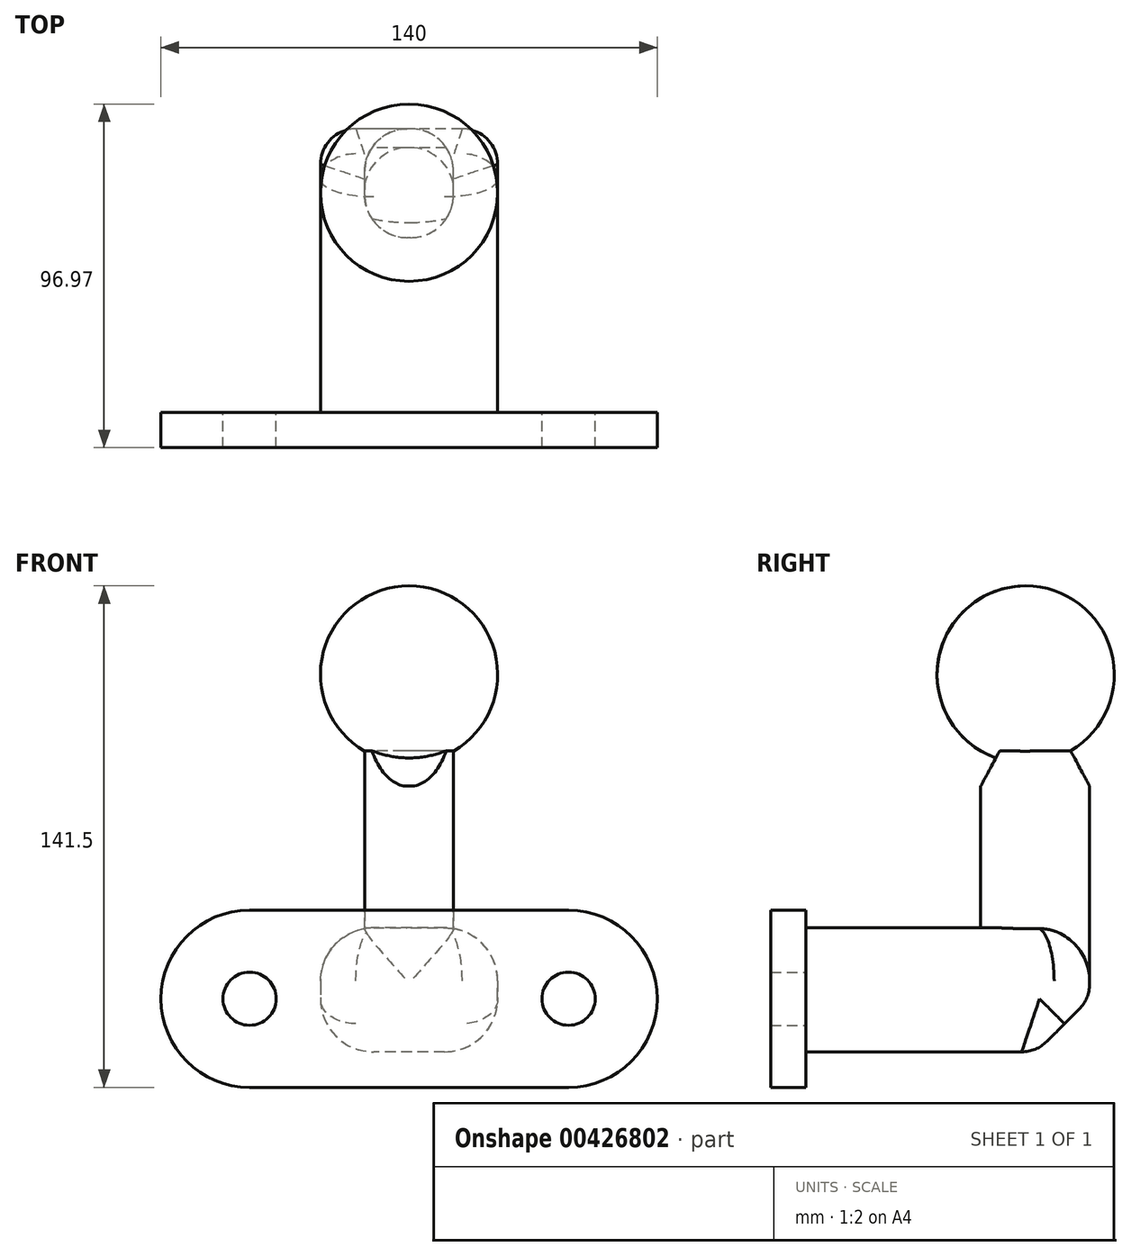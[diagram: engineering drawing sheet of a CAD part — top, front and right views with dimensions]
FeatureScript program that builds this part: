
annotation { "Feature Type Name" : "Feature", "Feature Type Description" : "" }
export const myFeature = defineFeature(function(context is Context, id is Id, definition is map)
    precondition{}
    {
        {
            var Q0;
            Q0=qCreatedBy(makeId("Front.planeOp"),FACE);
            var sketch = newSketch(context, id + "F0", { "sketchPlane" : qUnion([Q0])});
            skLineSegment(sketch, "E0.bottom", {"start": v(-45, 25) * mm, "end": v(45, 25) * mm});
            skLineSegment(sketch, "E0.top", {"start": v(-45, -25) * mm, "end": v(45, -25) * mm});
            skLineSegment(sketch, "E0.left", {"start": v(-70, 0) * mm, "end": v(-70, 0) * mm});
            skLineSegment(sketch, "E0.right", {"start": v(70, 0) * mm, "end": v(70, 0) * mm});
            skPoint(sketch, "E0.middle", {"position": v(0, 0) * mm});
            skCircle(sketch, "E1", {"center": v(-45, 0) * mm, "radius": 7.5 * mm});
            skCircle(sketch, "E2", {"center": v(45, 0) * mm, "radius": 7.5 * mm});
            skPoint(sketch, "E3.visualSharp", {"position": v(-70, 25) * mm});
            skArc(sketch, "E3.filletArc", {"start": v(-45, 25) * mm, "mid": v(-62.68, 17.68) * mm, "end": v(-70, 0) * mm});
            skPoint(sketch, "E4.visualSharp", {"position": v(-70, -25) * mm});
            skArc(sketch, "E4.filletArc", {"start": v(-70, 0) * mm, "mid": v(-62.68, -17.68) * mm, "end": v(-45, -25) * mm});
            skPoint(sketch, "E5.visualSharp", {"position": v(70, -25) * mm});
            skArc(sketch, "E5.filletArc", {"start": v(45, -25) * mm, "mid": v(62.68, -17.68) * mm, "end": v(70, 0) * mm});
            skPoint(sketch, "E6.visualSharp", {"position": v(70, 25) * mm});
            skArc(sketch, "E6.filletArc", {"start": v(70, 0) * mm, "mid": v(62.68, 17.68) * mm, "end": v(45, 25) * mm});
            skSolve(sketch);
        }
        {
            var Q0;
            Q0=makeQuery(id+"F0.imprint","IMPRINT",FACE,{"disambiguationData":[TD([[makeQuery(id+"F0.imprint","IMPRINT",EDGE,{"derivedFrom":sQuery(id+"F0.wireOp",EDGE,"E0.bottom")}),-1.0]])]});
            extrude(context, id + "F1", {"entities" : qUnion([Q0]), "depth" : 10 * mm});
        }
        {
            var Q0;
            Q0=qCreatedBy(makeId("Right.planeOp"),FACE);
            var sketch = newSketch(context, id + "F2", { "sketchPlane" : qUnion([Q0])});
            skLineSegment(sketch, "E7.bottom", {"start": v(0, 20) * mm, "end": v(80, 20) * mm});
            skLineSegment(sketch, "E7.top", {"start": v(0, -15) * mm, "end": v(80, -15) * mm});
            skLineSegment(sketch, "E7.left", {"start": v(0, 20) * mm, "end": v(0, -15) * mm});
            skLineSegment(sketch, "E7.right", {"start": v(80, 20) * mm, "end": v(80, -15) * mm});
            skLineSegment(sketch, "E8", {"start": v(80, 20) * mm, "end": v(80, 60) * mm});
            skLineSegment(sketch, "E9", {"start": v(64.64, 92.1) * mm, "end": v(64.64, 12.06) * mm, "construction": true});
            skLineSegment(sketch, "E10.MirrorCS", {"start": v(49.28, 20) * mm, "end": v(49.28, 60) * mm});
            skLineSegment(sketch, "E11", {"start": v(54.64, 70) * mm, "end": v(74.64, 70) * mm});
            skLineSegment(sketch, "E12", {"start": v(74.64, 70) * mm, "end": v(80, 60) * mm});
            skLineSegment(sketch, "E13", {"start": v(49.28, 60) * mm, "end": v(54.64, 70) * mm});
            skSolve(sketch);
        }
        {
            var Q0;
            Q0=makeQuery(id+"F2.imprint","IMPRINT",FACE,{"disambiguationData":[TD([[makeQuery(id+"F2.imprint","IMPRINT",EDGE,{"derivedFrom":sQuery(id+"F2.wireOp",EDGE,"E7.top")}),1.0]])]});
            extrude(context, id + "F3", {"entities" : qUnion([Q0]), "operationType" : NewBodyOperationType.ADD, "endBound" : BoundingType.SYMMETRIC, "depth" : 50 * mm});
        }
        {
            var Q0;
            Q0 = qSketchRegion(id + "F2", true);
            extrude(context, id + "F4", {"entities" : qUnion([Q0]), "operationType" : NewBodyOperationType.ADD, "endBound" : BoundingType.SYMMETRIC, "depth" : 25 * mm});
        }
        {
            var Q0;
            Q0=qCreatedBy(makeId("Right.planeOp"),FACE);
            var sketch = newSketch(context, id + "F5", { "sketchPlane" : qUnion([Q0])});
            skLineSegment(sketch, "E14", {"start": v(61.97, 66.5) * mm, "end": v(61.97, 91.5) * mm});
            skArc(sketch, "E15", {"start": v(61.97, 66.5) * mm, "mid": v(86.97, 91.5) * mm, "end": v(61.97, 116.5) * mm});
            skLineSegment(sketch, "E16", {"start": v(61.97, 91.5) * mm, "end": v(61.97, 116.5) * mm});
            skSolve(sketch);
        }
        {
            var Q0;
            Q0=makeQuery(id+"F5.imprint","IMPRINT",FACE,{"disambiguationData":[TD([[makeQuery(id+"F5.imprint","IMPRINT",EDGE,{"derivedFrom":sQuery(id+"F5.wireOp",EDGE,"E14")}),-1.0]])]});
            var Q1;
            Q1=sQuery(id+"F5.wireOp",EDGE,"E16");
            revolve(context, id + "F6", {"operationType" : NewBodyOperationType.ADD, "entities" : qUnion([Q0]), "axis" : qUnion([Q1]), "revolveType" : RevolveType.FULL});
        }
        {
            var Q0;
            Q0=makeQuery(id+"F4.opExtrude","CAP_EDGE",EDGE,{"disambiguationData":[OSD([sQuery(id+"F2.wireOp",EDGE,"E7.right"),sQuery(id+"F2.wireOp",EDGE,"E8")])],"isStart":true});
            var Q1;
            Q1=makeQuery(id+"F4.opExtrude","CAP_EDGE",EDGE,{"disambiguationData":[OSD([sQuery(id+"F2.wireOp",EDGE,"E7.right"),sQuery(id+"F2.wireOp",EDGE,"E8")])],"isStart":false});
            var Q2;
            Q2=makeQuery(id+"F4.opExtrude","CAP_EDGE",EDGE,{"disambiguationData":[OSD([sQuery(id+"F2.wireOp",EDGE,"E10.MirrorCS")])],"isStart":true});
            var Q3;
            Q3=makeQuery(id+"F4.opExtrude","CAP_EDGE",EDGE,{"disambiguationData":[OSD([sQuery(id+"F2.wireOp",EDGE,"E10.MirrorCS")])],"isStart":false});
            fillet(context, id + "F7", {"entities" : qUnion([Q0, Q1, Q2, Q3]), "radius" : 12 * mm, "tangentPropagation" : true, "allowEdgeOverflow" : false});
        }
        {
            var Q0;
            Q0=makeQuery(id+"F3.opExtrude","SWEPT_EDGE",EDGE,{"disambiguationData":[OSD([sQuery(id+"F2.wireOp",EDGE,"E7.top"),sQuery(id+"F2.wireOp",EDGE,"E7.right")])]});
            chamfer(context, id + "F8", {"entities" : qUnion([Q0]), "width" : 15 * mm, "tangentPropagation" : true});
        }
        {
            var Q0;
            {var subQ0=sQuery(id+"F2.wireOp",EDGE,"E7.right");Q0=makeQuery(id+"F8.opChamfer","BLEND_EDGE",EDGE,{"blendedFrom":[makeQuery(id+"F3.opExtrude","SWEPT_EDGE",EDGE,{"disambiguationData":[OSD([sQuery(id+"F2.wireOp",EDGE,"E7.top"),subQ0])]}),makeQuery(id+"F4.boolean.opBoolean","MERGE",FACE,{"derivedFrom":[makeQuery(id+"F3.opExtrude","SWEPT_FACE",FACE,{"disambiguationData":[OSD([subQ0])]}),makeQuery(id+"F4.opExtrude","SWEPT_FACE",FACE,{"disambiguationData":[OSD([subQ0,sQuery(id+"F2.wireOp",EDGE,"E8")])]})]})],"blendedInto":[makeQuery(id+"F4.boolean.opBoolean","MERGE",FACE,{"derivedFrom":[makeQuery(id+"F3.opExtrude","SWEPT_FACE",FACE,{"disambiguationData":[OSD([subQ0])]}),makeQuery(id+"F4.opExtrude","SWEPT_FACE",FACE,{"disambiguationData":[OSD([subQ0,sQuery(id+"F2.wireOp",EDGE,"E8")])]})]})]});}
            var Q1;
            {var subQ0=sQuery(id+"F2.wireOp",EDGE,"E7.top");Q1=makeQuery(id+"F8.opChamfer","BLEND_EDGE",EDGE,{"blendedFrom":[makeQuery(id+"F3.opExtrude","SWEPT_EDGE",EDGE,{"disambiguationData":[OSD([subQ0,sQuery(id+"F2.wireOp",EDGE,"E7.right")])]}),makeQuery(id+"F3.opExtrude","SWEPT_FACE",FACE,{"disambiguationData":[OSD([subQ0])]})],"blendedInto":[makeQuery(id+"F3.opExtrude","SWEPT_FACE",FACE,{"disambiguationData":[OSD([subQ0])]})]});}
            var Q2;
            Q2=makeQuery(id+"F3.opExtrude","CAP_EDGE",EDGE,{"disambiguationData":[OSD([sQuery(id+"F2.wireOp",EDGE,"E7.right")])],"isStart":false});
            var Q3;
            Q3=makeQuery(id+"F3.opExtrude","CAP_EDGE",EDGE,{"disambiguationData":[OSD([sQuery(id+"F2.wireOp",EDGE,"E7.right")])],"isStart":true});
            var Q4;
            {var subQ0=sQuery(id+"F2.wireOp",EDGE,"E7.right");var subQ1=sQuery(id+"F2.wireOp",EDGE,"E7.top");Q4=makeQuery(id+"F8.opChamfer","BLEND_EDGE",EDGE,{"blendedFrom":[makeQuery(id+"F3.opExtrude","SWEPT_EDGE",EDGE,{"disambiguationData":[OSD([subQ1,subQ0])]}),makeQuery(id+"F3.opExtrude","CAP_FACE",FACE,{"disambiguationData":[OSD([sQuery(id+"F2.wireOp",EDGE,"E7.bottom"),subQ1,sQuery(id+"F2.wireOp",EDGE,"E7.left"),subQ0])],"isStart":true})],"blendedInto":[makeQuery(id+"F3.opExtrude","CAP_FACE",FACE,{"disambiguationData":[OSD([sQuery(id+"F2.wireOp",EDGE,"E7.bottom"),subQ1,sQuery(id+"F2.wireOp",EDGE,"E7.left"),subQ0])],"isStart":true})]});}
            var Q5;
            {var subQ0=sQuery(id+"F2.wireOp",EDGE,"E7.right");var subQ1=sQuery(id+"F2.wireOp",EDGE,"E7.top");Q5=makeQuery(id+"F8.opChamfer","BLEND_EDGE",EDGE,{"blendedFrom":[makeQuery(id+"F3.opExtrude","SWEPT_EDGE",EDGE,{"disambiguationData":[OSD([subQ1,subQ0])]}),makeQuery(id+"F3.opExtrude","CAP_FACE",FACE,{"disambiguationData":[OSD([sQuery(id+"F2.wireOp",EDGE,"E7.bottom"),subQ1,sQuery(id+"F2.wireOp",EDGE,"E7.left"),subQ0])],"isStart":false})],"blendedInto":[makeQuery(id+"F3.opExtrude","CAP_FACE",FACE,{"disambiguationData":[OSD([sQuery(id+"F2.wireOp",EDGE,"E7.bottom"),subQ1,sQuery(id+"F2.wireOp",EDGE,"E7.left"),subQ0])],"isStart":false})]});}
            fillet(context, id + "F9", {"entities" : qUnion([Q0, Q1, Q2, Q3, Q4, Q5]), "radius" : 10 * mm, "tangentPropagation" : true, "allowEdgeOverflow" : false});
        }
        {
            var Q0;
            Q0=makeQuery(id+"F3.opExtrude","CAP_EDGE",EDGE,{"disambiguationData":[OSD([sQuery(id+"F2.wireOp",EDGE,"E7.bottom")])],"isStart":false});
            var Q1;
            Q1=makeQuery(id+"F3.opExtrude","CAP_EDGE",EDGE,{"disambiguationData":[OSD([sQuery(id+"F2.wireOp",EDGE,"E7.bottom")])],"isStart":true});
            var Q2;
            Q2=makeQuery(id+"F3.opExtrude","CAP_EDGE",EDGE,{"disambiguationData":[OSD([sQuery(id+"F2.wireOp",EDGE,"E7.top")])],"isStart":false});
            var Q3;
            Q3=makeQuery(id+"F3.opExtrude","CAP_EDGE",EDGE,{"disambiguationData":[OSD([sQuery(id+"F2.wireOp",EDGE,"E7.top")])],"isStart":true});
            fillet(context, id + "F10", {"entities" : qUnion([Q0, Q1, Q2, Q3]), "radius" : 15 * mm, "tangentPropagation" : true, "allowEdgeOverflow" : false});
        }
    });
